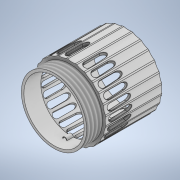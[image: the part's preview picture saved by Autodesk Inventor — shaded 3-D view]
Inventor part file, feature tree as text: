
AUTODESK INVENTOR PART (.ipt)
format: ipt  version: 2020.2 (Build 242310000, 310)  size: 3,676,160 bytes
history: native  units: mm
features: plane x14, sketch x11, extrude x9, chamfer x3, pattern_circular x3, mirror x2, emboss x1, revolve x1, split x1, thread x1, projected_geometry x1
ambient origin geometry x8: Origin, YZ Plane, XZ Plane, XY Plane, X Axis, Y Axis, Z Axis, Center Point
bodies: Solid1 (feature_tree), Solid2 (feature_tree), Solid3 (feature_tree)
feature tree (47):
  extrude  "Extrusion1"  Depth=2.0mm
  plane  "Work Plane1"
  sketch  "Sketch2"  dims[d2=4.714404mm d3=0.428883mm d4=250.0mm d6=360.0deg d8=45.0mm d9=0.0mm d11=10.0mm d12=0.0mm d15=250.0mm d16=360.0deg]
  extrude  "Extrusion2"  Depth=10.0mm
  chamfer  "Chamfer1"  Distance=250.0mm Angle=360.0deg
  chamfer  "Chamfer2"  Distance=45.0mm
  chamfer  "Chamfer3"  Distance=10.0mm
  pattern_circular  "Circular Pattern1"  Count=25 Angle=360.0deg
  plane  "Work Plane7"
  plane  "Work Plane8"
  plane  "Work Plane9"
  emboss  "Emboss1"
  revolve  "Revolution1"  Angle=45.0deg
  pattern_circular  "Circular Pattern2"  Count=4 Angle=360.0deg
  extrude  "Extrusion9"  Depth=21.5mm
  plane  "Work Plane10"
  plane  "Work Plane11"
  split  "Split1"
  extrude  "Extrusion11"  Depth=10.0mm
  thread  "Thread4"  [1 undecoded]
  plane  "Work Plane12"
  plane  "Work Plane14"
  extrude  "Extrusion12"  [1 undecoded]
  plane  "Work Plane15"
  mirror  "Mirror2"
  sketch  "Sketch21"  dims[d55=1.5mm d56=0.0mm d62=21.5mm d63=30.0mm]
  extrude  "Extrusion13"  Depth=0.5mm TaperAngle=0.0deg
  plane  "Work Plane16"
  sketch  "Sketch22"  dims[d64=0.02mm d65=1.586041mm d66=10.0mm d67=0.0mm]
  plane  "Work Plane17"
  extrude  "Extrusion14"  [1 undecoded]
  extrude  "Extrusion15"  Depth=2.5mm
  extrude  "Extrusion16"  Depth=2.5mm
  mirror  "Mirror3"
  pattern_circular  "Circular Pattern3"  [2 undecoded]
  sketch  "Sketch1"  dims[d0=45.0mm d1=2.0mm]
  plane  "Work Plane5"
  plane  "Work Plane6"
  sketch  "Sketch9"  dims[d18=0.9mm d19=2.0mm d20=45.0deg d21=0.9mm d22=2.0mm d23=45.0deg]
  sketch  "Sketch11"  dims[d24=0.2mm d25=2.0mm d26=45.0deg]
  sketch  "Sketch15"  dims[d37=11.75mm]
  sketch  "Sketch17"  dims[d38=-16.0mm d39=8.7mm d40=-8.7mm]
  sketch  "Sketch18"  dims[d41=0.2mm d42=0.0mm]
  plane  "Work Plane13"
  sketch  "Sketch20"  dims[d43=90.0deg d44=40.0mm d45=360.0deg]
  projected_geometry  "Projected Loop1"
  sketch  "Sketch23"  dims[d68=10.0mm d69=0.0mm d70=-2.25mm d71=0.5mm d72=0.0mm d73=-20.75mm d74=0.801779mm d75=2.939856mm d76=4.0mm d77=0.0mm d78=-1.25mm d79=2.5mm d80=0.0mm d81=1.75mm d82=0.0mm d83=2.0mm d84=0.0mm d85=20.0mm d86=360.0deg]
note: 5 required parameter values undecoded (feature->parameter linkage not recoverable at this tier; creation-order binding heuristic only, values carry confidence <= 0.55)
